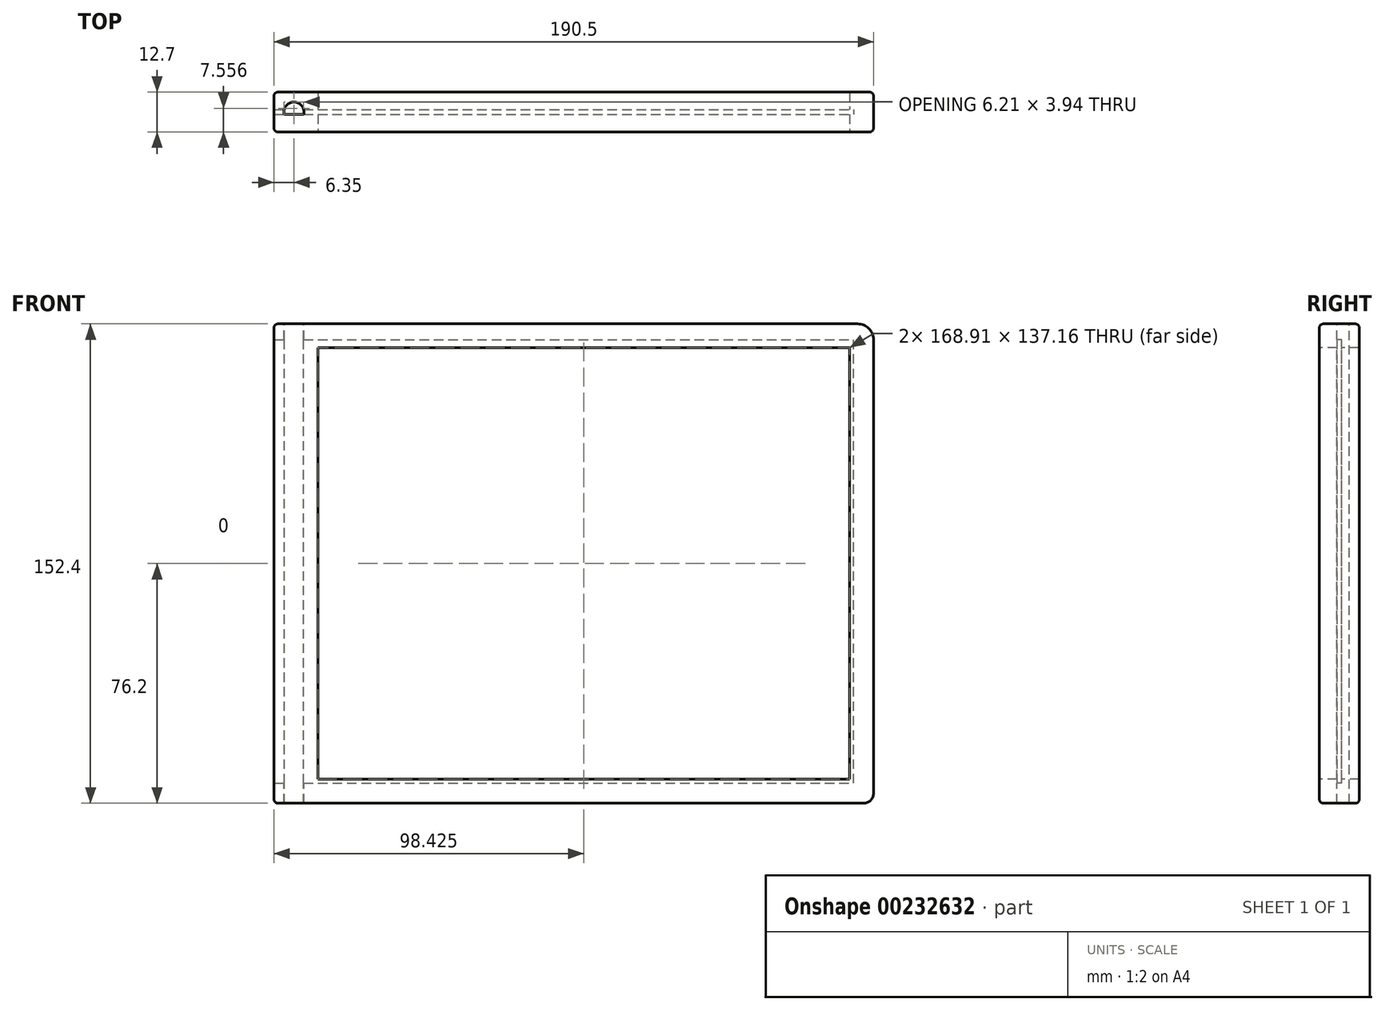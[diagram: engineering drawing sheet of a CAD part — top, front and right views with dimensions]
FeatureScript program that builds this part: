
annotation { "Feature Type Name" : "Feature", "Feature Type Description" : "" }
export const myFeature = defineFeature(function(context is Context, id is Id, definition is map)
    precondition{}
    {
        {
            var Q0;
            Q0=qCreatedBy(makeId("Front.planeOp"),FACE);
            var sketch = newSketch(context, id + "F0", { "sketchPlane" : qUnion([Q0])});
            skLineSegment(sketch, "E0.bottom", {"start": v(0, 0) * mm, "end": v(190.5, 0) * mm});
            skLineSegment(sketch, "E0.top", {"start": v(0, 152.4) * mm, "end": v(190.5, 152.4) * mm});
            skLineSegment(sketch, "E0.left", {"start": v(0, 0) * mm, "end": v(0, 152.4) * mm});
            skLineSegment(sketch, "E0.right", {"start": v(190.5, 0) * mm, "end": v(190.5, 152.4) * mm});
            skLineSegment(sketch, "E1.bottom", {"start": v(182.88, 144.78) * mm, "end": v(13.97, 144.78) * mm});
            skLineSegment(sketch, "E1.top", {"start": v(182.88, 7.62) * mm, "end": v(13.97, 7.62) * mm});
            skLineSegment(sketch, "E1.left", {"start": v(182.88, 144.78) * mm, "end": v(182.88, 7.62) * mm});
            skLineSegment(sketch, "E1.right", {"start": v(13.97, 144.78) * mm, "end": v(13.97, 7.62) * mm});
            skPoint(sketch, "E1.middle", {"position": v(98.43, 76.2) * mm});
            skLineSegment(sketch, "E2", {"start": v(190.5, 76.2) * mm, "end": v(182.88, 76.2) * mm, "construction": true});
            skSolve(sketch);
        }
        {
            var Q0;
            Q0=makeQuery(id+"F0.imprint","IMPRINT",FACE,{"disambiguationData":[TD([[makeQuery(id+"F0.imprint","IMPRINT",EDGE,{"derivedFrom":sQuery(id+"F0.wireOp",EDGE,"E0.bottom")}),1.0]])]});
            extrude(context, id + "F1", {"entities" : qUnion([Q0]), "oppositeDirection" : true, "depth" : 12.7 * mm});
        }
        {
            var Q0;
            Q0=makeQuery(id+"F1.opExtrude","SWEPT_FACE",FACE,{"disambiguationData":[OSD([sQuery(id+"F0.wireOp",EDGE,"E0.top")])]});
            var sketch = newSketch(context, id + "F2", { "sketchPlane" : qUnion([Q0])});
            skCircle(sketch, "E3", {"center": v(6.35, 6.35) * mm, "radius": 3.18 * mm});
            skLineSegment(sketch, "E4", {"start": v(0, 6.35) * mm, "end": v(6.35, 6.35) * mm, "construction": true});
            skLineSegment(sketch, "E5.bottom", {"start": v(-69.85, 7.11) * mm, "end": v(184.15, 7.11) * mm});
            skLineSegment(sketch, "E5.top", {"start": v(-69.85, 5.59) * mm, "end": v(184.15, 5.59) * mm});
            skLineSegment(sketch, "E5.left", {"start": v(-69.85, 7.11) * mm, "end": v(-69.85, 5.59) * mm});
            skLineSegment(sketch, "E5.right", {"start": v(184.15, 7.11) * mm, "end": v(184.15, 5.59) * mm});
            skLineSegment(sketch, "E6", {"start": v(184.15, 6.35) * mm, "end": v(190.5, 6.35) * mm, "construction": true});
            skPoint(sketch, "E6.endSnap0", {"position": v(184.15, 6.35) * mm});
            skLineSegment(sketch, "E7", {"start": v(6.35, 6.35) * mm, "end": v(-69.85, 6.35) * mm, "construction": true});
            skSolve(sketch);
        }
        {
            var Q0;
            Q0=makeQuery(id+"F1.opExtrude","SWEPT_EDGE",EDGE,{"disambiguationData":[OSD([sQuery(id+"F0.wireOp",EDGE,"E0.top"),sQuery(id+"F0.wireOp",EDGE,"E0.right")])]});
            fillet(context, id + "F3", {"entities" : qUnion([Q0]), "radius" : 5.08 * mm, "tangentPropagation" : true, "allowEdgeOverflow" : false});
        }
        {
            var Q0;
            Q0=makeQuery(id+"F1.opExtrude","SWEPT_EDGE",EDGE,{"disambiguationData":[OSD([sQuery(id+"F0.wireOp",EDGE,"E0.bottom"),sQuery(id+"F0.wireOp",EDGE,"E0.right")])]});
            fillet(context, id + "F4", {"entities" : qUnion([Q0]), "radius" : 3.17 * mm, "tangentPropagation" : true, "allowEdgeOverflow" : false});
        }
        {
            var Q0;
            Q0=makeQuery(id+"F1.opExtrude","CAP_EDGE",EDGE,{"disambiguationData":[OSD([sQuery(id+"F0.wireOp",EDGE,"E0.left")])],"isStart":true});
            var Q1;
            Q1=makeQuery(id+"F1.opExtrude","CAP_EDGE",EDGE,{"disambiguationData":[OSD([sQuery(id+"F0.wireOp",EDGE,"E0.left")])],"isStart":false});
            fillet(context, id + "F5", {"entities" : qUnion([Q0, Q1]), "radius" : 1.27 * mm, "tangentPropagation" : true, "allowEdgeOverflow" : false});
        }
        {
            var Q0;
            Q0=makeQuery(id+"F1.opExtrude","CAP_EDGE",EDGE,{"disambiguationData":[OSD([sQuery(id+"F0.wireOp",EDGE,"E0.top")])],"isStart":true});
            var Q1;
            {var subQ0=sQuery(id+"F0.wireOp",EDGE,"E0.left");Q1=makeQuery(id+"F5.opFillet","BLEND_EDGE",EDGE,{"blendedFrom":[makeQuery(id+"F1.opExtrude","CAP_EDGE",EDGE,{"disambiguationData":[OSD([subQ0])],"isStart":true}),makeQuery(id+"F1.opExtrude","CAP_FACE",FACE,{"disambiguationData":[OSD([sQuery(id+"F0.wireOp",EDGE,"E0.bottom"),sQuery(id+"F0.wireOp",EDGE,"E0.top"),subQ0,sQuery(id+"F0.wireOp",EDGE,"E0.right"),sQuery(id+"F0.wireOp",EDGE,"E1.bottom"),sQuery(id+"F0.wireOp",EDGE,"E1.top"),sQuery(id+"F0.wireOp",EDGE,"E1.left"),sQuery(id+"F0.wireOp",EDGE,"E1.right")])],"isStart":true})],"blendedInto":[makeQuery(id+"F1.opExtrude","CAP_FACE",FACE,{"disambiguationData":[OSD([sQuery(id+"F0.wireOp",EDGE,"E0.bottom"),sQuery(id+"F0.wireOp",EDGE,"E0.top"),subQ0,sQuery(id+"F0.wireOp",EDGE,"E0.right"),sQuery(id+"F0.wireOp",EDGE,"E1.bottom"),sQuery(id+"F0.wireOp",EDGE,"E1.top"),sQuery(id+"F0.wireOp",EDGE,"E1.left"),sQuery(id+"F0.wireOp",EDGE,"E1.right")])],"isStart":true})]});}
            fillet(context, id + "F6", {"entities" : qUnion([Q0, Q1]), "radius" : 1.27 * mm, "tangentPropagation" : true, "allowEdgeOverflow" : false});
        }
        {
            var Q0;
            Q0=makeQuery(id+"F2.imprint","IMPRINT",FACE,{"disambiguationData":[TD([[makeQuery(id+"F2.imprint","IMPRINT",EDGE,{"derivedFrom":sQuery(id+"F2.wireOp",EDGE,"E5.bottom")}),-1.0]])]});
            extrude(context, id + "F7", {"entities" : qUnion([Q0]), "operationType" : NewBodyOperationType.REMOVE, "oppositeDirection" : true, "depth" : 146.05 * mm, "hasSecondDirection" : true, "secondDirectionOppositeDirection" : true, "secondDirectionDepth" : 5.08 * mm});
        }
        {
            var Q0;
            {var subQ0=sQuery(id+"F2.wireOp",EDGE,"E5.bottom");var subQ1=sQuery(id+"F2.wireOp",EDGE,"E3");var subQ2=makeQuery(id+"F2.imprint","INTERSECT",VERTEX,{"disambiguationData":[OD(0.0)],"derivedFrom":[subQ1,subQ0]});Q0=makeQuery(id+"F2.imprint","IMPRINT",FACE,{"disambiguationData":[TD([[makeQuery(id+"F2.imprint","IMPRINT",EDGE,{"disambiguationData":[TD([[subQ2,1.0]])],"derivedFrom":subQ1}),1.0]])]});}
            var Q1;
            {var subQ0=sQuery(id+"F2.wireOp",EDGE,"E5.top");var subQ1=sQuery(id+"F2.wireOp",EDGE,"E3");var subQ2=makeQuery(id+"F2.imprint","INTERSECT",VERTEX,{"disambiguationData":[OD(0.0)],"derivedFrom":[subQ1,subQ0]});Q1=makeQuery(id+"F2.imprint","IMPRINT",FACE,{"disambiguationData":[TD([[makeQuery(id+"F2.imprint","IMPRINT",EDGE,{"disambiguationData":[TD([[subQ2,-1.0]])],"derivedFrom":subQ1}),1.0]])]});}
            var Q2;
            {var subQ0=sQuery(id+"F2.wireOp",EDGE,"E5.bottom");var subQ1=sQuery(id+"F2.wireOp",EDGE,"E3");var subQ2=makeQuery(id+"F2.imprint","INTERSECT",VERTEX,{"disambiguationData":[OD(0.0)],"derivedFrom":[subQ1,subQ0]});Q2=makeQuery(id+"F2.imprint","IMPRINT",FACE,{"disambiguationData":[TD([[makeQuery(id+"F2.imprint","IMPRINT",EDGE,{"disambiguationData":[TD([[subQ2,-1.0]])],"derivedFrom":subQ1}),1.0]])]});}
            extrude(context, id + "F8", {"entities" : qUnion([Q0, Q1, Q2]), "operationType" : NewBodyOperationType.REMOVE, "endBound" : BoundingType.THROUGH_ALL, "oppositeDirection" : true, "depth" : 152.4 * mm});
        }
    });
